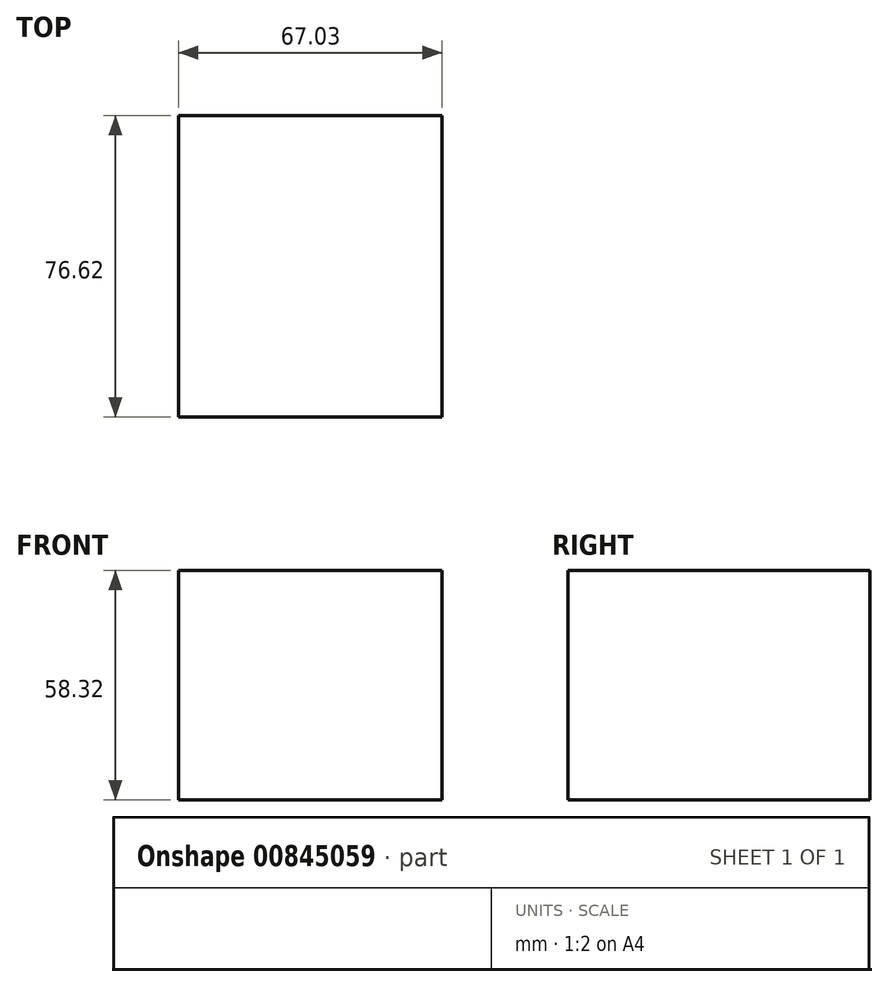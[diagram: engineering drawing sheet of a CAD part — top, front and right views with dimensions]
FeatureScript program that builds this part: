
annotation { "Feature Type Name" : "Feature", "Feature Type Description" : "" }
export const myFeature = defineFeature(function(context is Context, id is Id, definition is map)
    precondition{}
    {
        {
            var Q0;
            Q0=qCreatedBy(makeId("Top.planeOp"),FACE);
            var sketch = newSketch(context, id + "F0", { "sketchPlane" : qUnion([Q0])});
            skLineSegment(sketch, "E0.bottom", {"start": v(0, 0) * mm, "end": v(67.03, 0) * mm});
            skLineSegment(sketch, "E0.top", {"start": v(0, 76.62) * mm, "end": v(67.03, 76.62) * mm});
            skLineSegment(sketch, "E0.left", {"start": v(0, 0) * mm, "end": v(0, 76.62) * mm});
            skLineSegment(sketch, "E0.right", {"start": v(67.03, 0) * mm, "end": v(67.03, 76.62) * mm});
            skSolve(sketch);
        }
        {
            var Q0;
            Q0 = qSketchRegion(id + "F0", true);
            extrude(context, id + "F1", {"entities" : qUnion([Q0]), "depth" : 58.32 * mm, "offsetDistance" : 25.4 * mm});
        }
    });
